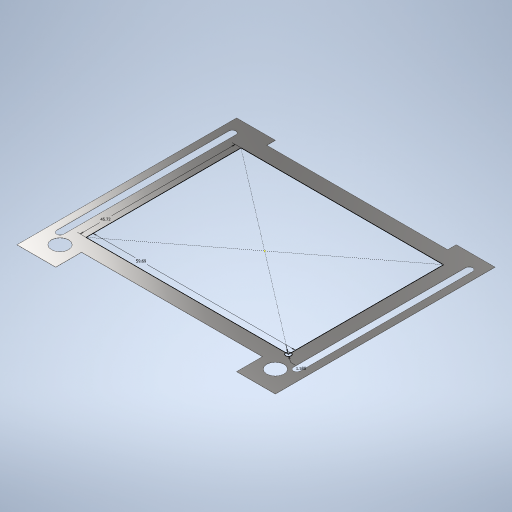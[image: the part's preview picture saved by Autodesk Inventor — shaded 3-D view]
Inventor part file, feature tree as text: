
AUTODESK INVENTOR PART (.ipt)
format: ipt  version: 2023 (Build 270158000, 158)  size: 332,288 bytes
history: native  units: in
note: dims shown in document units (in); Inventor stores cm internally (conversion verified against a paired STEP export)
features: sketch x6, extrude x5, hole x1
ambient origin geometry x8: Origin, YZ Plane, XZ Plane, XY Plane, X Axis, Y Axis, Z Axis, Center Point
bodies: Solid1 (feature_tree)
feature tree (12):
  extrude  "Extrusion1"  Depth=2.75in
  extrude  "Extrusion2"  Depth=0.08in
  extrude  "Extrusion3"  Depth=0.125in
  hole  "Hole1"  [1 undecoded]
  extrude  "Extrusion4"  Depth=0.45in
  extrude  "Extrusion5"  Depth=2.35in
  sketch  "Sketch1"  dims[d0=3.0in d1=2.75in]
  sketch  "Sketch2"  dims[d2=0.002in d3=0.0in d4=0.08in]
  sketch  "Sketch3"  dims[d5=0.125in d6=2.0in]
  sketch  "Sketch4"  dims[d7=0.0in d8=0.0in d9=0.3in]
  sketch  "Sketch5"  dims[d10=2.1in d11=0.45in]
  sketch  "Sketch6"  dims[d12=0.0in d13=0.0in d14=0.25in d15=0.25in d16=0.25in d17=0.25in d18=0.25in d19=0.25in d20=0.25in d21=0.25in d22=0.2in d23=0.75in d24=0.156in d25=0.073in d26=0.5635in d27=1.0in d28=0.8108in d29=0.2in d30=0.0in d31=0.0in d32=0.0625in d33=1.8in d34=2.35in d35=0.0in d36=0.0in]
note: 1 required parameter value undecoded (feature->parameter linkage not recoverable at this tier; creation-order binding heuristic only, values carry confidence <= 0.55)
